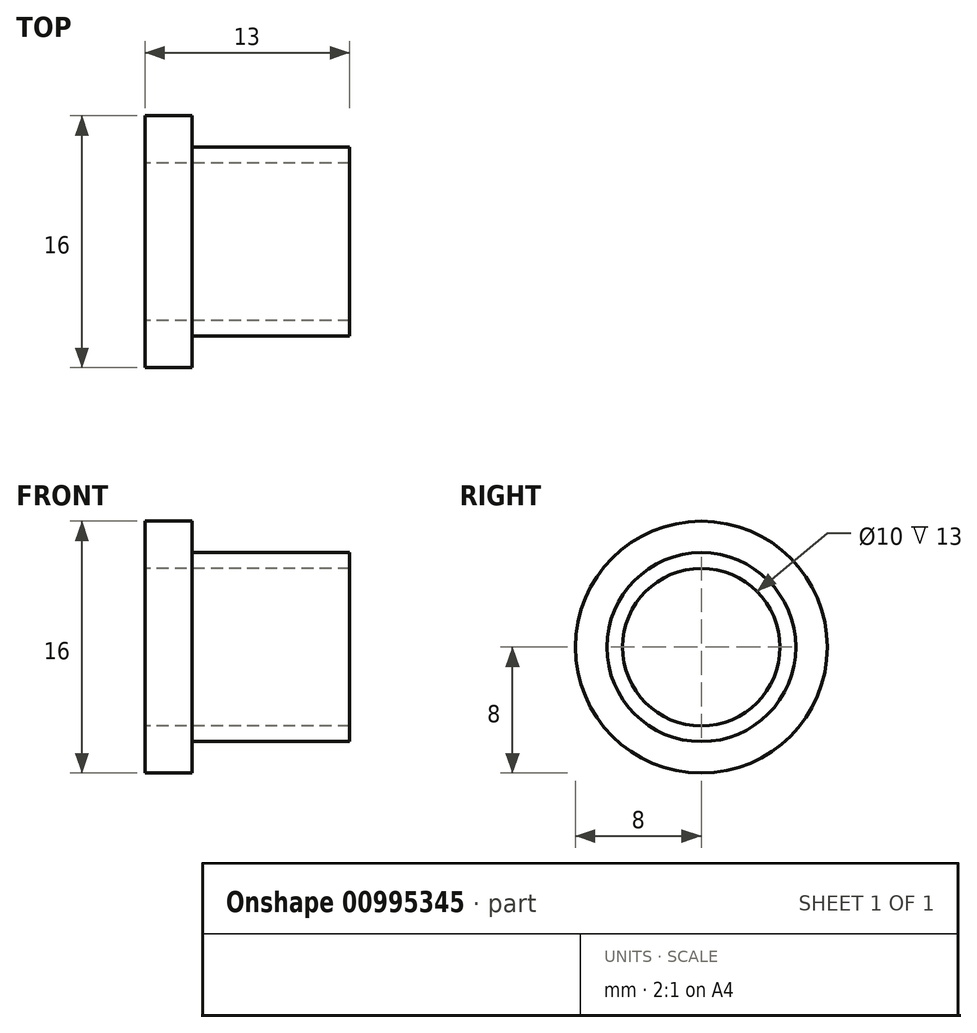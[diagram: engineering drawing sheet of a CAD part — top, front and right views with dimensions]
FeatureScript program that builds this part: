
annotation { "Feature Type Name" : "Feature", "Feature Type Description" : "" }
export const myFeature = defineFeature(function(context is Context, id is Id, definition is map)
    precondition{}
    {
        {
            var Q0;
            Q0=qCreatedBy(makeId("Front.planeOp"),FACE);
            var sketch = newSketch(context, id + "F0", { "sketchPlane" : qUnion([Q0])});
            skLineSegment(sketch, "E0", {"start": v(0, 5) * mm, "end": v(0, 8) * mm});
            skLineSegment(sketch, "E1", {"start": v(0, 8) * mm, "end": v(3, 8) * mm});
            skLineSegment(sketch, "E2", {"start": v(3, 8) * mm, "end": v(3, 6) * mm});
            skLineSegment(sketch, "E3", {"start": v(3, 6) * mm, "end": v(13, 6) * mm});
            skLineSegment(sketch, "E4", {"start": v(13, 6) * mm, "end": v(13, 5) * mm});
            skLineSegment(sketch, "E5", {"start": v(13, 5) * mm, "end": v(0, 5) * mm});
            skLineSegment(sketch, "E6", {"start": v(0, 0) * mm, "end": v(50, 0) * mm});
            skSolve(sketch);
        }
        {
            var Q0;
            Q0=makeQuery(id+"F0.imprint","IMPRINT",FACE,{"disambiguationData":[TD([[makeQuery(id+"F0.imprint","IMPRINT",EDGE,{"derivedFrom":sQuery(id+"F0.wireOp",EDGE,"E0")}),-1.0]])]});
            var Q1;
            Q1=sQuery(id+"F0.wireOp",EDGE,"E6");
            revolve(context, id + "F1", {"surfaceOperationType" : NewSurfaceOperationType.NEW, "entities" : qUnion([Q0]), "axis" : qUnion([Q1]), "revolveType" : RevolveType.FULL});
        }
    });
